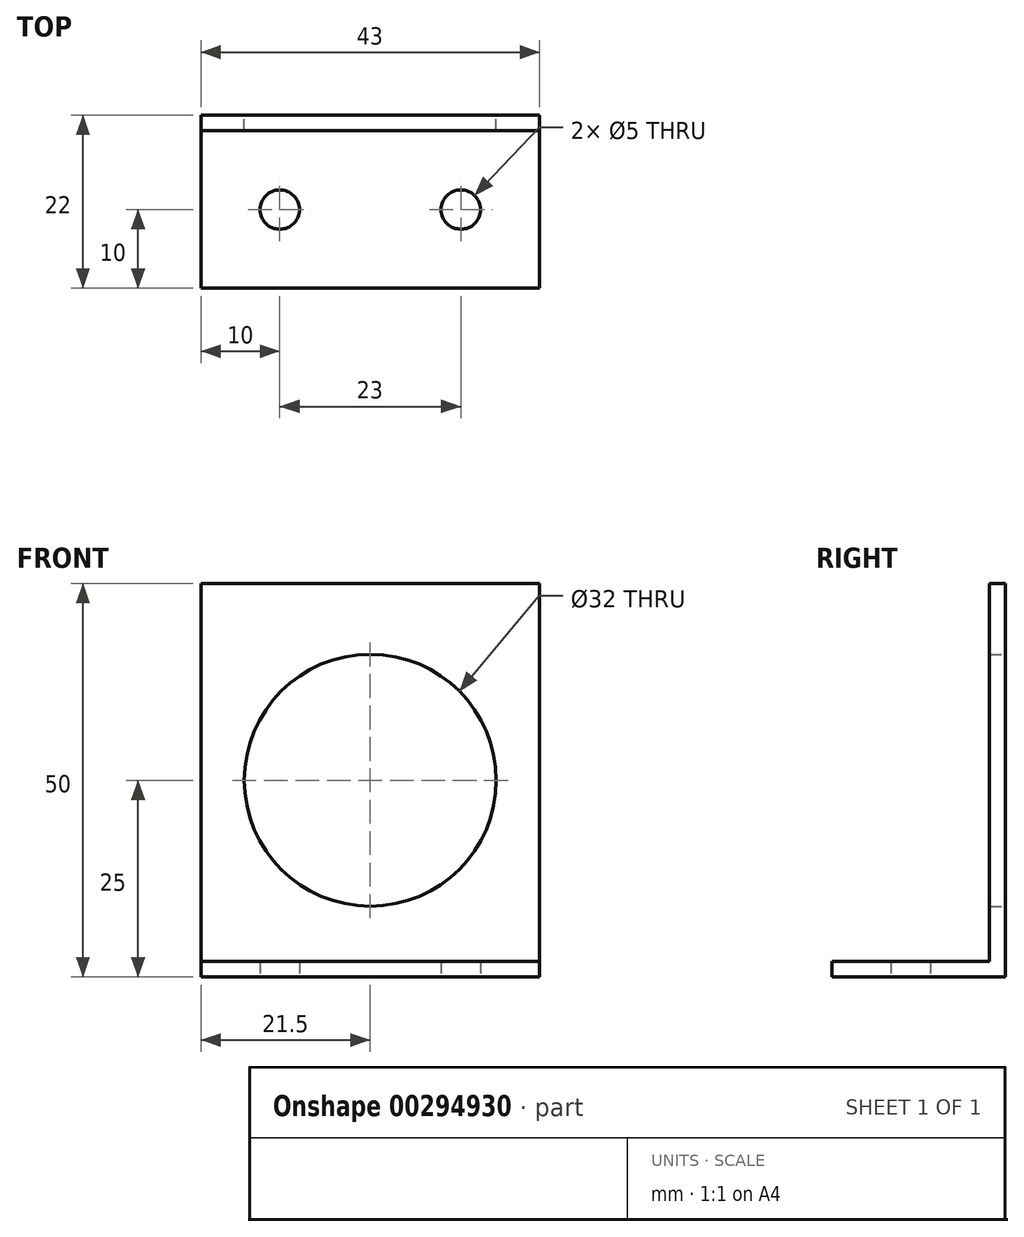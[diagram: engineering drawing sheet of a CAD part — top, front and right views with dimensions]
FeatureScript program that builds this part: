
annotation { "Feature Type Name" : "Feature", "Feature Type Description" : "" }
export const myFeature = defineFeature(function(context is Context, id is Id, definition is map)
    precondition{}
    {
        {
            var Q0;
            Q0=qCreatedBy(makeId("Front.planeOp"),FACE);
            var sketch = newSketch(context, id + "F0", { "sketchPlane" : qUnion([Q0])});
            skLineSegment(sketch, "E0.bottom", {"start": v(21.5, 25) * mm, "end": v(-21.5, 25) * mm});
            skLineSegment(sketch, "E0.top", {"start": v(21.5, -25) * mm, "end": v(-21.5, -25) * mm});
            skLineSegment(sketch, "E0.left", {"start": v(21.5, 25) * mm, "end": v(21.5, -25) * mm});
            skLineSegment(sketch, "E0.right", {"start": v(-21.5, 25) * mm, "end": v(-21.5, -25) * mm});
            skPoint(sketch, "E0.middle", {"position": v(0, 0) * mm});
            skCircle(sketch, "E1", {"center": v(0, 0) * mm, "radius": 16 * mm});
            skSolve(sketch);
        }
        {
            var Q0;
            Q0=makeQuery(id+"F0.imprint","IMPRINT",FACE,{"disambiguationData":[TD([[makeQuery(id+"F0.imprint","IMPRINT",EDGE,{"derivedFrom":sQuery(id+"F0.wireOp",EDGE,"E0.bottom")}),1.0]])]});
            extrude(context, id + "F1", {"entities" : qUnion([Q0]), "depth" : 2 * mm});
        }
        {
            var Q0;
            Q0=makeQuery(id+"F1.opExtrude","CAP_FACE",FACE,{"disambiguationData":[OSD([sQuery(id+"F0.wireOp",EDGE,"E0.bottom"),sQuery(id+"F0.wireOp",EDGE,"E0.top"),sQuery(id+"F0.wireOp",EDGE,"E0.left"),sQuery(id+"F0.wireOp",EDGE,"E0.right"),sQuery(id+"F0.wireOp",EDGE,"E1")])],"isStart":false});
            var sketch = newSketch(context, id + "F2", { "sketchPlane" : qUnion([Q0])});
            skLineSegment(sketch, "E2.bottom", {"start": v(-21.5, -25) * mm, "end": v(21.5, -25) * mm});
            skLineSegment(sketch, "E2.top", {"start": v(-21.5, -23) * mm, "end": v(21.5, -23) * mm});
            skLineSegment(sketch, "E2.left", {"start": v(-21.5, -25) * mm, "end": v(-21.5, -23) * mm});
            skLineSegment(sketch, "E2.right", {"start": v(21.5, -25) * mm, "end": v(21.5, -23) * mm});
            skSolve(sketch);
        }
        {
            var Q0;
            Q0=makeQuery(id+"F2.imprint","IMPRINT",FACE,{"disambiguationData":[TD([[makeQuery(id+"F2.imprint","IMPRINT",EDGE,{"derivedFrom":sQuery(id+"F2.wireOp",EDGE,"E2.bottom")}),-1.0]])]});
            extrude(context, id + "F3", {"entities" : qUnion([Q0]), "operationType" : NewBodyOperationType.ADD, "depth" : 20 * mm});
        }
        {
            var Q0;
            Q0=makeQuery(id+"F3.boolean.opBoolean","MERGE",FACE,{"derivedFrom":[makeQuery(id+"F1.opExtrude","SWEPT_FACE",FACE,{"disambiguationData":[OSD([sQuery(id+"F0.wireOp",EDGE,"E0.top")])]}),makeQuery(id+"F3.opExtrude","SWEPT_FACE",FACE,{"disambiguationData":[OSD([sQuery(id+"F2.wireOp",EDGE,"E2.bottom")])]})]});
            var sketch = newSketch(context, id + "F4", { "sketchPlane" : qUnion([Q0])});
            skPoint(sketch, "E3", {"position": v(-11.5, 12) * mm});
            skPoint(sketch, "E4", {"position": v(11.5, 12) * mm});
            skSolve(sketch);
        }
        {
            var Q0;
            Q0=sQuery(id+"F4.wireOp",VERTEX,"E3");
            var Q1;
            Q1=sQuery(id+"F4.wireOp",VERTEX,"E4");
            var Q2;
            Q2=makeQuery(id+"F1.opExtrude","SWEPT_BODY",BODY,{"disambiguationData":[OSD([sQuery(id+"F0.wireOp",EDGE,"E0.bottom"),sQuery(id+"F0.wireOp",EDGE,"E0.top"),sQuery(id+"F0.wireOp",EDGE,"E0.left"),sQuery(id+"F0.wireOp",EDGE,"E0.right"),sQuery(id+"F0.wireOp",EDGE,"E1")])]});
            hole(context, id + "F5", {"style" : HoleStyle.SIMPLE, "endStyle" : HoleEndStyle.THROUGH, "holeDiameter" : 5 * mm, "tappedDepth" : 12 * mm, "tapClearance" : 3, "locations" : qUnion([Q0, Q1]), "scope" : qUnion([Q2])});
        }
    });
